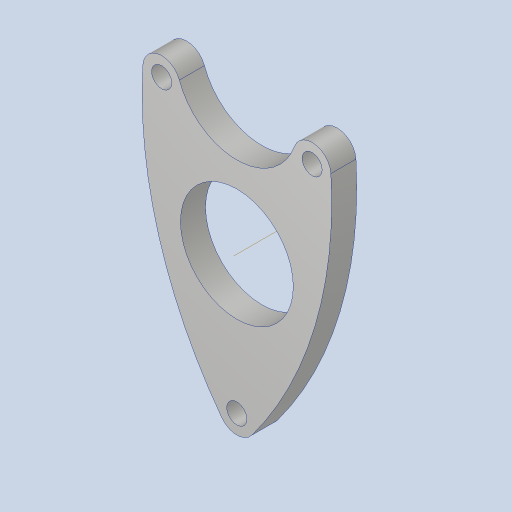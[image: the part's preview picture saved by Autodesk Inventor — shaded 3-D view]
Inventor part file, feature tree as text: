
AUTODESK INVENTOR PART (.ipt)
format: ipt  version: 2023.4 (Build 274418000, 418)  size: 138,240 bytes
history: native  units: in
note: dims shown in document units (in); Inventor stores cm internally (conversion verified against a paired STEP export)
features: sketch x1, extrude x1, hole x1, other x1
ambient origin geometry x8: Origin, YZ Plane, XZ Plane, XY Plane, X Axis, Y Axis, Z Axis, Center Point
bodies: Solid1 (feature_tree)
feature tree (4):
  sketch  "Sketch1"  dims[d0=1.125in d1=0.25in d2=0.375in d3=0.375in d4=0.375in d7=0.375in d8=0.375in d9=0.375in d13=0.75in d14=0.25in d15=0.0in d16=0.201in d17=0.75in d18=0.385in d19=0.25in d20=0.5635in d21=1.0in d22=0.8108in]
  extrude  "Extrusion1"  Depth=0.25in
  hole  "Hole1"  [1 undecoded]
  other  "Work Axis1"
note: 1 required parameter value undecoded (feature->parameter linkage not recoverable at this tier; creation-order binding heuristic only, values carry confidence <= 0.55)
